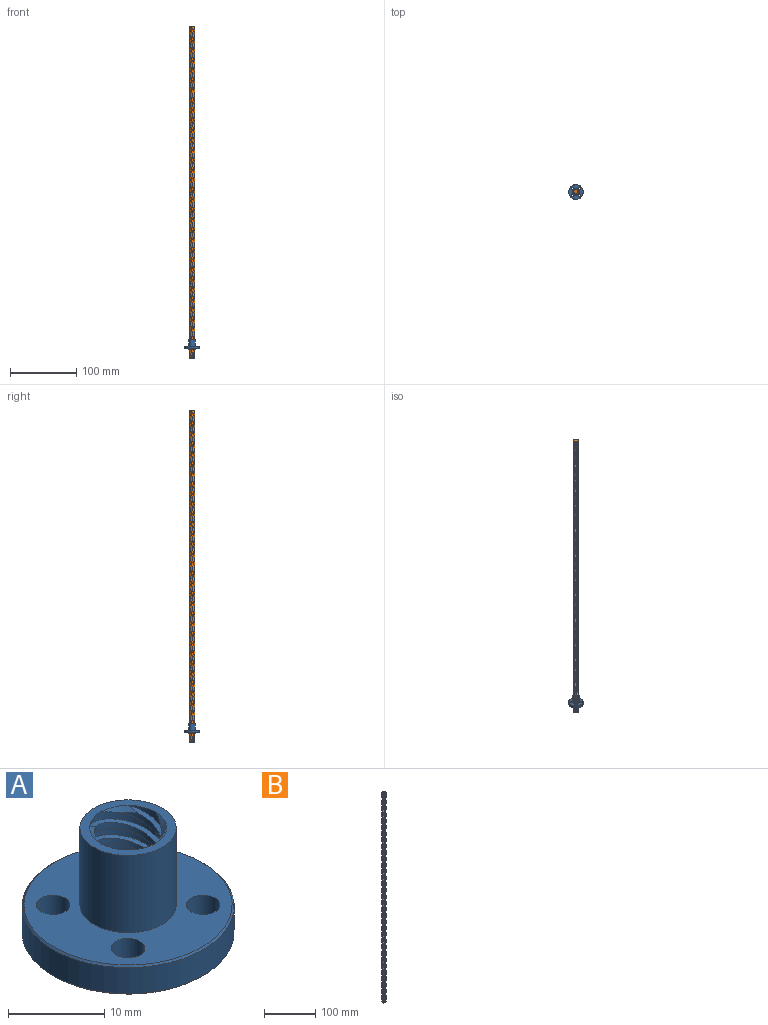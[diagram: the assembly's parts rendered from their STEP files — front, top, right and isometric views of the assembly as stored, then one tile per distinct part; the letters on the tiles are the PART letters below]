
ASSEMBLY  parts=2 mates=1
PART A: 37 faces, bbox 22x22x17.4 mm
  f0: cylinder r=1.75mm len=3.7mm, axis (0,0,-1), area 40.7mm2, adj f5,f6
  f1: cylinder r=1.75mm len=3.7mm, axis (0,0,-1), area 40.7mm2, adj f5,f6
  f2: cylinder r=1.75mm len=3.7mm, axis (0,0,-1), area 40.7mm2, adj f5,f6
  f3: cylinder r=1.75mm len=3.7mm, axis (0,0,-1), area 40.7mm2, adj f5,f6
  f4: cylinder r=11mm len=22mm, axis (0,0,-1), area 228.1mm2, adj f27,f28
  f5: plane 21.6x21.6mm, normal (0,0,1), area 249.4mm2, adj f0,f1,f2,f3,f9,f28
  f6: plane 21.6x21.6mm, normal (0,0,-1), area 249.4mm2, adj f0,f1,f2,f3,f8,f27
  f7: plane 10x10mm, normal (0,0,-1), area 28.3mm2, adj f8,f11,f15,f19,f23,f29,f30,f31
  f8: cylinder r=5mm len=10mm, axis (0,0,-1), area 47.1mm2, adj f6,f7
  f9: cylinder r=5mm len=10mm, axis (0,0,-1), area 307.9mm2, adj f5,f10
  f10: plane 10x10mm, normal (0,0,1), area 28.3mm2, adj f9,f11,f15,f19,f23,f33,f34,f35
  f11: cylinder r=4mm len=15mm, axis (0,0,-1), area 47.1mm2, adj f7,f10,f14,f16
  f12: bspline ~16.13x8mm, area 23.3mm2, adj f13,f23,f30,f36
  f13: cylinder r=3.5mm len=14mm, axis (0,0,1), area 28.2mm2, adj f12,f14,f30,f36
  f14: bspline ~17.4x9mm, area 23.3mm2, adj f11,f13,f30,f36
  f15: cylinder r=4mm len=15mm, axis (0,0,-1), area 47.1mm2, adj f7,f10,f18,f20
  f16: bspline ~16.13x8mm, area 23.3mm2, adj f11,f17,f29,f35
  f17: cylinder r=3.5mm len=14mm, axis (0,0,1), area 28.2mm2, adj f16,f18,f29,f35
  f18: bspline ~17.4x9mm, area 23.3mm2, adj f15,f17,f29,f35
  f19: cylinder r=4mm len=15mm, axis (0,0,-1), area 47.1mm2, adj f7,f10,f22,f25
  f20: bspline ~16.13x8mm, area 23.3mm2, adj f15,f21,f32,f34
  f21: cylinder r=3.5mm len=14mm, axis (0,0,1), area 28.2mm2, adj f20,f22,f32,f34
  f22: bspline ~17.4x9mm, area 23.3mm2, adj f19,f21,f32,f34
  f23: cylinder r=4mm len=15mm, axis (0,0,-1), area 47.1mm2, adj f7,f10,f12,f26
  f24: cylinder r=3.5mm len=14mm, axis (0,0,1), area 28.2mm2, adj f25,f26,f31,f33
  f25: bspline ~16.13x8mm, area 23.3mm2, adj f19,f24,f31,f33
  f26: bspline ~17.4x9mm, area 23.3mm2, adj f23,f24,f31,f33
  f27: cone r=11mm half-angle=45deg, axis (0,0,1), area 19.4mm2, adj f4,f6
  f28: cone r=10.8mm half-angle=45deg, axis (0,0,-1), area 19.4mm2, adj f4,f5
  f29: cone r=4mm half-angle=45deg, axis (0,0,-1), area 1.8mm2, adj f7,f16,f17,f18
  f30: cone r=4mm half-angle=45deg, axis (0,0,-1), area 1.8mm2, adj f7,f12,f13,f14
  f31: cone r=4mm half-angle=45deg, axis (0,0,-1), area 1.8mm2, adj f7,f24,f25,f26
  f32: cone r=4mm half-angle=45deg, axis (0,0,-1), area 1.8mm2, adj f7,f20,f21,f22
  f33: cone r=3.5mm half-angle=45deg, axis (0,0,1), area 1.8mm2, adj f10,f24,f25,f26
  f34: cone r=3.5mm half-angle=45deg, axis (0,0,1), area 1.8mm2, adj f10,f20,f21,f22
  f35: cone r=3.5mm half-angle=45deg, axis (0,0,1), area 1.8mm2, adj f10,f16,f17,f18
  f36: cone r=3.5mm half-angle=45deg, axis (0,0,1), area 1.8mm2, adj f10,f12,f13,f14
PART B: 26 faces, bbox 3471.7x3471.7x966 mm
  f0: cone r=4mm half-angle=45deg, axis (0,0,1), area 2.4mm2, adj f3,f18,f19,f23
  f1: cylinder r=4mm len=499mm, axis (0,0,-1), area 1576.8mm2, adj f5,f6,f8,f9
  f2: cone r=3.5mm half-angle=45deg, axis (0,0,-1), area 2.3mm2, adj f3,f19,f20,f23
  f3: bspline ~501.13x8mm, area 803.5mm2, adj f0,f2,f4,f19
  f4: cylinder r=3.5mm len=500mm, axis (0,0,1), area 3651.2mm2, adj f3,f5,f18,f20
  f5: bspline ~1740.35x966.04mm, area 800.6mm2, adj f1,f4,f6,f8
  f6: cone r=4mm half-angle=45deg, axis (0,0,1), area 2.4mm2, adj f1,f5,f9,f18
  f7: cylinder r=4mm len=499mm, axis (0,0,-1), area 1576.8mm2, adj f11,f12,f14,f15
  f8: cone r=3.5mm half-angle=45deg, axis (0,0,-1), area 2.3mm2, adj f1,f5,f9,f20
  f9: bspline ~501.13x8mm, area 803.5mm2, adj f1,f6,f8,f10
  f10: cylinder r=3.5mm len=500mm, axis (0,0,1), area 3651.2mm2, adj f9,f11,f18,f20
  f11: bspline ~1740.35x966.04mm, area 800.6mm2, adj f7,f10,f12,f14
  f12: cone r=4mm half-angle=45deg, axis (0,0,1), area 2.4mm2, adj f7,f11,f15,f18
  f13: cylinder r=4mm len=499mm, axis (0,0,-1), area 1576.8mm2, adj f17,f22,f24,f25
  f14: cone r=3.5mm half-angle=45deg, axis (0,0,-1), area 2.3mm2, adj f7,f11,f15,f20
  f15: bspline ~501.13x8mm, area 803.5mm2, adj f7,f12,f14,f16
  f16: cylinder r=3.5mm len=500mm, axis (0,0,1), area 3651.2mm2, adj f15,f17,f18,f20
  f17: bspline ~1740.35x966.04mm, area 800.6mm2, adj f13,f16,f24,f25
  f18: plane 7x7mm, normal (0,0,-1), area 38.5mm2, adj f0,f4,f6,f10,f12,f16,f21,f25
  f19: cylinder r=4mm len=499mm, axis (0,0,-1), area 1576.8mm2, adj f0,f2,f3,f23
  f20: plane 7x7mm, normal (0,0,1), area 38.5mm2, adj f2,f4,f8,f10,f14,f16,f21,f24
  f21: cylinder r=3.5mm len=500mm, axis (0,0,1), area 3651.2mm2, adj f18,f20,f22,f23
  f22: bspline ~501.13x8mm, area 803.5mm2, adj f13,f21,f24,f25
  f23: bspline ~1740.35x966.04mm, area 800.6mm2, adj f0,f2,f19,f21
  f24: cone r=3.5mm half-angle=45deg, axis (0,0,-1), area 2.3mm2, adj f13,f17,f20,f22
  f25: cone r=4mm half-angle=45deg, axis (0,0,1), area 2.4mm2, adj f13,f17,f18,f22
PLACE A t=(0,0,-6.5)mm fixed
PLACE B rot(axis=(0,0,-1),92.3deg) t=(0,0,-12.45)mm
MATE cylindrical B.f0 <-> A.f4  axis (0,0,-1) through (0,0,-12.45)mm
